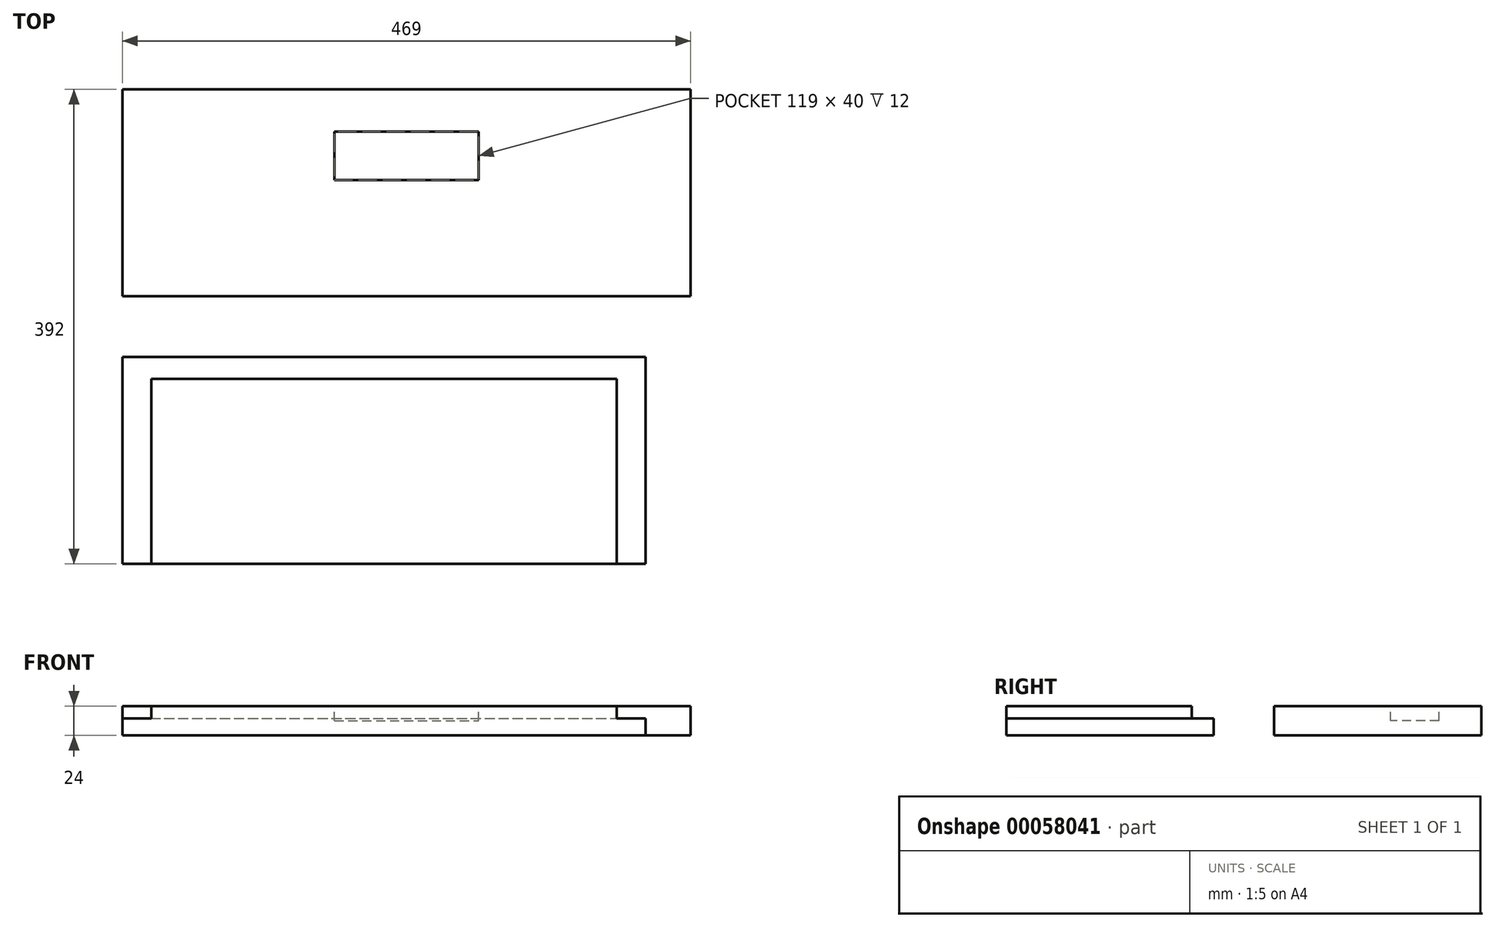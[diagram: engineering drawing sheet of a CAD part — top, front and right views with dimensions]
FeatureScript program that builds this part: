
annotation { "Feature Type Name" : "Feature", "Feature Type Description" : "" }
export const myFeature = defineFeature(function(context is Context, id is Id, definition is map)
    precondition{}
    {
        {
            var Q0;
            Q0=qCreatedBy(makeId("Top.planeOp"),FACE);
            var sketch = newSketch(context, id + "F0", { "sketchPlane" : qUnion([Q0])});
            skLineSegment(sketch, "E0.bottom", {"start": v(0, 0) * mm, "end": v(432, 0) * mm});
            skLineSegment(sketch, "E0.top", {"start": v(0, -171) * mm, "end": v(432, -171) * mm});
            skLineSegment(sketch, "E0.left", {"start": v(0, 0) * mm, "end": v(0, -171) * mm});
            skLineSegment(sketch, "E0.right", {"start": v(432, 0) * mm, "end": v(432, -171) * mm});
            skSolve(sketch);
        }
        {
            var Q0;
            Q0 = qSketchRegion(id + "F0", true);
            var Q1;
            Q1=makeQuery(id+"F0.imprint","IMPRINT",FACE,{"disambiguationData":[TD([[makeQuery(id+"F0.imprint","IMPRINT",EDGE,{"derivedFrom":sQuery(id+"F0.wireOp",EDGE,"E0.bottom")}),-1.0]])]});
            extrude(context, id + "F1", {"entities" : qUnion([Q0, Q1]), "depth" : 24 * mm});
        }
        {
            var Q0;
            Q0=makeQuery(id+"F1.opExtrude","CAP_FACE",FACE,{"disambiguationData":[OSD([sQuery(id+"F0.wireOp",EDGE,"E0.bottom"),sQuery(id+"F0.wireOp",EDGE,"E0.top"),sQuery(id+"F0.wireOp",EDGE,"E0.left"),sQuery(id+"F0.wireOp",EDGE,"E0.right")])],"isStart":false});
            var sketch = newSketch(context, id + "F2", { "sketchPlane" : qUnion([Q0])});
            skLineSegment(sketch, "E1", {"start": v(0, -171) * mm, "end": v(24, -171) * mm});
            skLineSegment(sketch, "E2", {"start": v(24, -171) * mm, "end": v(24, -18) * mm});
            skLineSegment(sketch, "E3", {"start": v(24, -18) * mm, "end": v(408, -18) * mm});
            skLineSegment(sketch, "E4", {"start": v(408, -18) * mm, "end": v(408, -171) * mm});
            skLineSegment(sketch, "E5", {"start": v(408, -171) * mm, "end": v(432, -171) * mm});
            skLineSegment(sketch, "E6", {"start": v(432, -171) * mm, "end": v(432, 0) * mm});
            skLineSegment(sketch, "E7", {"start": v(432, 0) * mm, "end": v(0, 0) * mm});
            skLineSegment(sketch, "E8", {"start": v(0, 0) * mm, "end": v(0, -171) * mm});
            skSolve(sketch);
        }
        {
            var Q0;
            Q0 = qSketchRegion(id + "F2", true);
            extrude(context, id + "F3", {"entities" : qUnion([Q0]), "operationType" : NewBodyOperationType.REMOVE, "oppositeDirection" : true, "depth" : 10 * mm});
        }
        {
            var Q0;
            Q0=qCreatedBy(makeId("Top.planeOp"),FACE);
            var sketch = newSketch(context, id + "F4", { "sketchPlane" : qUnion([Q0])});
            skLineSegment(sketch, "E9.bottom", {"start": v(0, 221) * mm, "end": v(469, 221) * mm});
            skLineSegment(sketch, "E9.top", {"start": v(0, 50) * mm, "end": v(469, 50) * mm});
            skLineSegment(sketch, "E9.left", {"start": v(0, 221) * mm, "end": v(0, 50) * mm});
            skLineSegment(sketch, "E9.right", {"start": v(469, 221) * mm, "end": v(469, 50) * mm});
            skSolve(sketch);
        }
        {
            var Q0;
            Q0=makeQuery(id+"F4.imprint","IMPRINT",FACE,{"disambiguationData":[TD([[makeQuery(id+"F4.imprint","IMPRINT",EDGE,{"derivedFrom":sQuery(id+"F4.wireOp",EDGE,"E9.bottom")}),-1.0]])]});
            extrude(context, id + "F5", {"entities" : qUnion([Q0]), "depth" : 24 * mm});
        }
        {
            var Q0;
            Q0=makeQuery(id+"F5.opExtrude","CAP_FACE",FACE,{"disambiguationData":[OSD([sQuery(id+"F4.wireOp",EDGE,"E9.bottom"),sQuery(id+"F4.wireOp",EDGE,"E9.top"),sQuery(id+"F4.wireOp",EDGE,"E9.left"),sQuery(id+"F4.wireOp",EDGE,"E9.right")])],"isStart":false});
            var sketch = newSketch(context, id + "F6", { "sketchPlane" : qUnion([Q0])});
            skLineSegment(sketch, "E10.bottom", {"start": v(175, 186) * mm, "end": v(294, 186) * mm});
            skLineSegment(sketch, "E10.top", {"start": v(175, 146) * mm, "end": v(294, 146) * mm});
            skLineSegment(sketch, "E10.left", {"start": v(175, 186) * mm, "end": v(175, 146) * mm});
            skLineSegment(sketch, "E10.right", {"start": v(294, 186) * mm, "end": v(294, 146) * mm});
            skSolve(sketch);
        }
        {
            var Q0;
            Q0 = qSketchRegion(id + "F6", true);
            extrude(context, id + "F7", {"entities" : qUnion([Q0]), "operationType" : NewBodyOperationType.REMOVE, "oppositeDirection" : true, "depth" : 12 * mm});
        }
    });
